# Revit family: GIRA_210800
name_source: partatom
category: Elektroinstallationen
revit_build: Autodesk Revit 2017 (Build: 20160225_1515(x64)
units: mm (PartAtom-declared; Revit-internal decimal feet)

## family parameters
Basisbauteil = Fläche
Beim Laden mit Abzugskörper schneiden = Nein
Bemaßung runder Anschluss = Durchmesser verwenden
Beschriftungsausrichtung beibehalten = Nein
Gemeinsam genutzt = Nein
Raumberechnungspunkt = Nein
Teiletyp = Normal

## types (1)
- GIRA_210800
    Andere Bussysteme Text = sonstige
    Anzahl der Ausgänge = 2
    Anzahl der Ausgänge Number = 6
    Ausführung Text = Medienkoppler
    Ausgangsleistung [Watt] = [20:500]
    Bemessungsstrom = 16 A
    Beschreibung = KNX DALI-Gateway Tunable White Plus   Merkmale: - Steuern von Leuchten und anderen Anwendungen mit DALI-Betriebsgerät in KNX Installationen. - Einstellung der Farbtemperatur für Leuchten mit DALI Device Type 8 (Clour Type: Colour Temperatur) für Tunable White gemäß IEC 62386-209. - Kurzschlussschutz, Überspannungsschutz, Überlastschutz. - Schalten und Dimmen von maximal 64 Leuchten mit DALI-Betriebsgeräten. - Bis zu 6 unterschiedliche Adressierungsarten ermöglichen das gruppenorientierte und einzeladressierte Ansteuern von DALI-Leuchten über KNX Telegramme. - Bei Gruppenadressierung stehen bis zu 32 unabhängige DALI-Gruppen zur Verfügung. Diese können um 64 einzeladressierbare DALI-Gerätekanäle ergänzt werden. - Ansteuerung von DALI-Betriebsgeräten des Gerätetyps Colour Control" (DALI Device Type 8, Colour Type: Colour Temperature) in der spezifischen Ausprägung "Tunable White (TW)". Steuerung der Farbtemperatur über relatives oder absolutes Dimmen und zusätzlich über Szenen und Effekte. - Zentralsteuerung aller angeschlossenen DALI-Komponenten möglich (Broadcast). - Handbetätigung unabhängig vom Bus (Baustellenbetrieb mit Broadcast-Steuerung). Steuerung des Schaltzustands und der Helligkeit. - Rückmeldungen von DALI-Fehlerstatus oder DALI-Kurzschluss und Meldung von Ausfall der Versorgungsspannung. - Zentrale Schaltfunktion. - Sammelrückmeldung aller Schaltzustände möglich. - 16 Lichtszenen. - Effektsteuerung zur Realisierung dynamischer Lichtstimmungen. 16 Effekte mit jeweils bis zu 16 Effekt-Schritten. Timer mit dem sich Effekte abhängig von Uhrzeit und Wochentag starten und stoppen lassen. Gruppen- und Gerätefunktionen: - Schalten und Helligkeitswert: Aktive oder passive Rückmeldefunktionen. - Einstellung der Helligkeitsgrenzwerte (Minimal- bzw. Maximalhelligkeit). - Dimmverhalten und Dimmkennlinien parametrierbar. - Lampenschonendes Ein- und Ausschalten. - Sperrfunktion oder Zwangsstellungsfunktion parametrierbar. - Zeitfunktionen (Ein-, Ausschaltverzögerung, Treppenhausfunktion - auch mit Vorwarnfunktion). - Betriebsstundenzähler. - DALI-Power-ON-Level und DALI-System-Failure-Level einstellbar. - Reaktionen bei Busspannungsausfall und -wiederkehr und nach ETS-Programmiervorgang einstellbar. - Steuerung der Farbtemperatur über absolutes Dimmen und relatives Dimmen, parametrierbares Dimmverhalten, minimale und maximale Farbtemperatur einstellbar, Rückmeldungen für aktuelle und ungültige Farbtemperatur. Betrieb von Notleuchten: - Einbindung des Geräts in DALI-Notlichtsysteme. Das DALI-Gateway ist in der Lage, DALI-Standardbetriebsgeräte für Beleuchtungssteuerungen gemäß IEC 62386-101 (DALI-System) und IEC 62386-102 (Control-Gear) als Notleuchte in zentralversorgte Notlichtsysteme zu integrieren. - Überwachung auf Ausfall der allgemeinen Spannungsversorgung. - Verhalten am Ende des Notbetriebs einstellbar. - Helligkeit und Farbtemperatur bei aktivem Notbetrieb einstellbar. ETS-Plug-in: - DALI-Inbetriebnahme ohne zusätzliche Softwarekomponenten. Das Identifizieren, Adressieren und Zuordnen von DALI-Betriebsgeräten erfolgt im ETS-Plug-in. - Zuordnen von Einzelgeräten zu Gruppen auch ohne Programmierverbindung zum Gerät. - Kompatibilitätsprüfung der DALI-Gerätetypen bei der Zuordnen von DALI-Betriebsgeräten. - Kompatibilitätsmodus zur Unterstützung nicht DALI-konformer Betriebsgeräte. - Partielle DALI-Inbetriebnahme. - Testfunktion aller angelegten DALI-Gruppen oder DALI-Betriebsgeräte. - Exportieren und Importieren einer Vorlage. - Druckfunktion zur Erstellung eines Reports.  Hinweise : - Betrieb von Notbeleuchtungsanlagen:   Die gesetzlichen und normativen Vorgaben sind länderspezifisch unterschiedlich. Es ist in jedem Fall durch den Anwender   Fachplaner zu prüfen, ob die spezifischen Vorgaben eingehalten werden. - VDE-Zulassung gemäß EN 60669-1, EN 60669-2-1. - Projektierung und Inbetriebnahme des Geräts ab ETS 4.2 oder ETS 5 (Empfehlung). - Der Gira AppShop ist der Marktplatz für interessante Lösungen und Anwendungen der intelligenten Gebäudetechnik. Inzwischen sind dort mehr als 200 Apps erhältlich, darunter Anwendungsbeschreibungen, Plug-ins, Funktionsvorlagen, Logikbausteine und Musterprojekte. Entdecken Sie jetzt Anwendungen für das KNX DALI-Gateway Tunable White Plus.   www.appshop.gira.de."
    Breite in Teilungseinheiten = 4
    Breite in Teilungseinheiten Number = 4
    Busmodul abnehmbar = Nein
    Busmodul abnehmbar YesNo = Nein
    Bussystem Funkbus YesNo = Nein
    Bussystem KNX YesNo = Ja
    Bussystem KNX-Funk YesNo = Nein
    Bussystem LON YesNo = Nein
    Bussystem Powernet YesNo = Nein
    Demontageschutz = Nein
    Frequenz [Hz] = [50:60]
    Funk bidirektional = Nein
    Funk bidirektional YesNo = Nein
    GTIN = 4010337032878
    HAN = 210800
    Handschaltung = Ja
    Hersteller = Gira
    IR-Schnittstelle = Nein
    Lastart = universal
    Leistungszusatz verwendbar = Nein
    Max. Anzahl der Jalousieausgänge = 4
    Max. Anzahl der Schaltausgänge = 8
    Max. Schaltstrom (Ohmsche Last) = 2 A
    Mit Busankopplung YesNo = Nein
    Mit LED-Anzeige = Nein
    Mit LED-Anzeige YesNo = Nein
    Modulare Erweiterungsmöglichkeit = Ja
    Montageart Text = REG
    Nebenstelleneingang = Ja
    Parallel-Betrieb möglich = Nein
    Schaltspannung [Volt] = [110:230]
    Schutzart (IP) Text = IP20
    Spannung [Volt] = [230:230]
    Stellgröße schaltend = Nein
    Stellgröße stetig = Ja
    Typname = DALI-Gateway Tunable WH Plus KNX REG
    URL = https://www.gira.de
    Ventilschutzfunktion = Nein
    Vor Ort-/Handbedienung = Ja
    Vor Ort-/Handbedienung YesNo = Ja
    Vorgabe-Ansicht = 1219 mm

## geometry (parser evidence)
native form markers: Sweep x3
no freeform markers — native parametric forms only
